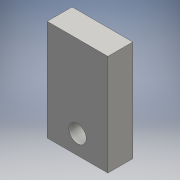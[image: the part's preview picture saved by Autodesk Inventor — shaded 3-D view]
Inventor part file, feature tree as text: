
AUTODESK INVENTOR PART (.ipt)
format: ipt  version: 2016 (Build 200138000, 138)  size: 98,304 bytes
history: native  units: mm
features: extrude x2, sketch x2, projected_geometry x1
ambient origin geometry x8: Origin, YZ Plane, XZ Plane, XY Plane, X Axis, Y Axis, Z Axis, Center Point
bodies: Solid1 (feature_tree)
feature tree (5):
  extrude  "Extrusion1"  Depth=5.0038mm TaperAngle=0.0deg
  extrude  "Extrusion2"  Depth=0.25mm
  sketch  "Sketch1"  dims[d0=5.0038mm d1=0.0mm d2=10.16mm d3=0.0mm]
  sketch  "Sketch2"  dims[d4=0.25mm d5=0.25mm]
  projected_geometry  "Projected Loop1"
